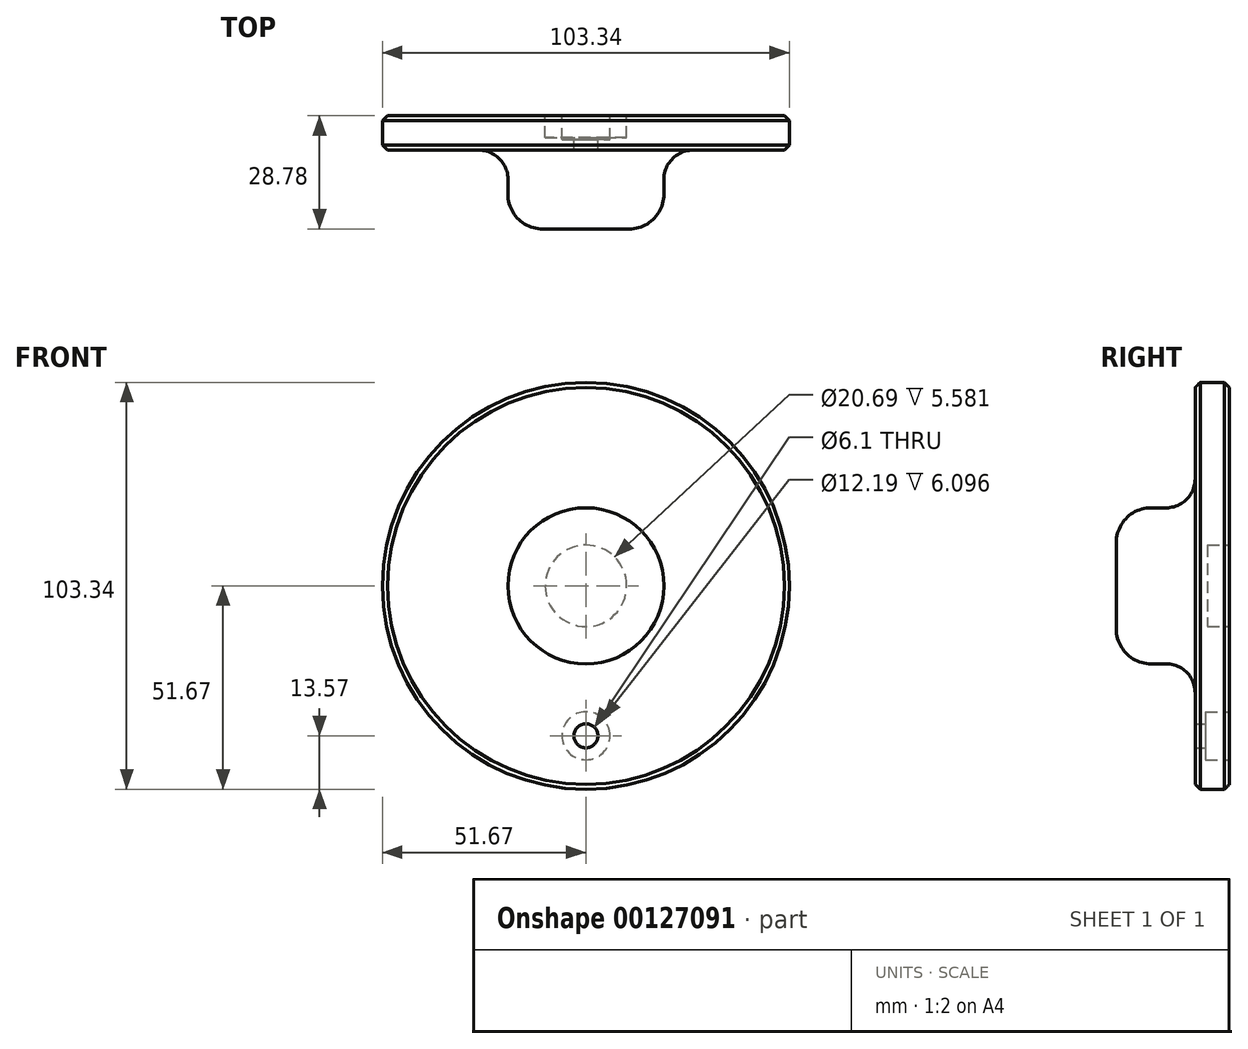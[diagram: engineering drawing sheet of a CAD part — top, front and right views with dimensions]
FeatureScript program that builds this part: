
annotation { "Feature Type Name" : "Feature", "Feature Type Description" : "" }
export const myFeature = defineFeature(function(context is Context, id is Id, definition is map)
    precondition{}
    {
        {
            var Q0;
            Q0=qCreatedBy(makeId("Top.planeOp"),FACE);
            var sketch = newSketch(context, id + "F0", { "sketchPlane" : qUnion([Q0])});
            skLineSegment(sketch, "E0", {"start": v(0, 0) * mm, "end": v(0, 40.3) * mm, "construction": true});
            skSolve(sketch);
        }
        {
            var Q0;
            Q0=qCreatedBy(makeId("Top.planeOp"),FACE);
            var sketch = newSketch(context, id + "F1", { "sketchPlane" : qUnion([Q0])});
            skLineSegment(sketch, "E1", {"start": v(0, 0) * mm, "end": v(19.82, 0) * mm});
            skLineSegment(sketch, "E2", {"start": v(19.82, 0) * mm, "end": v(19.82, 20.03) * mm});
            skLineSegment(sketch, "E3", {"start": v(19.82, 20.03) * mm, "end": v(51.67, 20.03) * mm});
            skLineSegment(sketch, "E4", {"start": v(51.67, 20.03) * mm, "end": v(51.67, 28.78) * mm});
            skLineSegment(sketch, "E5", {"start": v(51.67, 28.78) * mm, "end": v(10.34, 28.78) * mm});
            skLineSegment(sketch, "E6", {"start": v(10.34, 28.78) * mm, "end": v(10.34, 23.2) * mm});
            skLineSegment(sketch, "E7", {"start": v(10.34, 23.2) * mm, "end": v(0, 23.2) * mm});
            skLineSegment(sketch, "E8", {"start": v(0, 23.2) * mm, "end": v(0, 0) * mm});
            skLineSegment(sketch, "E9", {"start": v(0, 23.2) * mm, "end": v(0, 29.85) * mm, "construction": true});
            skSolve(sketch);
        }
        {
            var Q0;
            Q0=makeQuery(id+"F1.imprint","IMPRINT",FACE,{"disambiguationData":[TD([[makeQuery(id+"F1.imprint","IMPRINT",EDGE,{"derivedFrom":sQuery(id+"F1.wireOp",EDGE,"E1")}),1.0]])]});
            var Q1;
            Q1=sQuery(id+"F1.wireOp",EDGE,"E9");
            var Q2;
            Q2=sQuery(id+"F1.wireOp",EDGE,"E6");
            var Q3;
            Q3=sQuery(id+"F1.wireOp",EDGE,"E5");
            var Q4;
            Q4=sQuery(id+"F1.wireOp",EDGE,"E4");
            var Q5;
            Q5=sQuery(id+"F1.wireOp",EDGE,"E3");
            var Q6;
            Q6=sQuery(id+"F1.wireOp",EDGE,"E2");
            var Q7;
            Q7=sQuery(id+"F1.wireOp",EDGE,"E1");
            var Q8;
            Q8=sQuery(id+"F1.wireOp",EDGE,"E7");
            var Q9;
            Q9=sQuery(id+"F1.wireOp",EDGE,"E8");
            revolve(context, id + "F2", {"entities" : qUnion([Q0]), "surfaceEntities" : qUnion([Q1, Q2, Q3, Q4, Q5, Q6, Q7, Q8]), "axis" : qUnion([Q9]), "revolveType" : RevolveType.FULL});
        }
        {
            var Q0;
            Q0=makeQuery(id+"F2.opRevolve","SWEPT_FACE",FACE,{"disambiguationData":[OSD([sQuery(id+"F1.wireOp",EDGE,"E5")])]});
            var sketch = newSketch(context, id + "F3", { "sketchPlane" : qUnion([Q0])});
            skLineSegment(sketch, "E10", {"start": v(0, 0) * mm, "end": v(0, -63.16) * mm, "construction": true});
            skCircle(sketch, "E11", {"center": v(0, 0) * mm, "radius": 38.1 * mm, "construction": true});
            skCircle(sketch, "E12", {"center": v(0, -38.1) * mm, "radius": 6.36 * mm});
            skSolve(sketch);
        }
        {
            var Q0;
            Q0=sQuery(id+"F3.wireOp",VERTEX,"E12.center");
            var Q1;
            Q1=makeQuery(id+"F2.opRevolve","SWEPT_BODY",BODY,{"disambiguationData":[OSD([sQuery(id+"F1.wireOp",EDGE,"E1"),sQuery(id+"F1.wireOp",EDGE,"E2"),sQuery(id+"F1.wireOp",EDGE,"E3"),sQuery(id+"F1.wireOp",EDGE,"E4"),sQuery(id+"F1.wireOp",EDGE,"E5"),sQuery(id+"F1.wireOp",EDGE,"E6"),sQuery(id+"F1.wireOp",EDGE,"E7"),sQuery(id+"F1.wireOp",EDGE,"E8")])]});
            hole(context, id + "F4", {"style" : HoleStyle.C_BORE, "endStyle" : HoleEndStyle.THROUGH, "holeDiameter" : 6.1 * mm, "cBoreDiameter" : 12.2 * mm, "cBoreDepth" : 6.1 * mm, "isTappedThrough" : true, "tappedDepth" : 12.2 * mm, "tapClearance" : 3, "startFromSketch" : true, "locations" : qUnion([Q0]), "scope" : qUnion([Q1])});
        }
        {
            var Q0;
            Q0=makeQuery(id+"F2.opRevolve","SWEPT_EDGE",EDGE,{"disambiguationData":[OSD([sQuery(id+"F1.wireOp",EDGE,"E2"),sQuery(id+"F1.wireOp",EDGE,"E3")])]});
            fillet(context, id + "F5", {"entities" : qUnion([Q0]), "radius" : 7.36 * mm, "tangentPropagation" : true, "allowEdgeOverflow" : false});
        }
        {
            var Q0;
            Q0=makeQuery(id+"F2.opRevolve","SWEPT_EDGE",EDGE,{"disambiguationData":[OSD([sQuery(id+"F1.wireOp",EDGE,"E1"),sQuery(id+"F1.wireOp",EDGE,"E2")])]});
            fillet(context, id + "F6", {"entities" : qUnion([Q0]), "radius" : 8.83 * mm, "tangentPropagation" : true, "allowEdgeOverflow" : false});
        }
        {
            var Q0;
            Q0=makeQuery(id+"F2.opRevolve","SWEPT_EDGE",EDGE,{"disambiguationData":[OSD([sQuery(id+"F1.wireOp",EDGE,"E3"),sQuery(id+"F1.wireOp",EDGE,"E4")])]});
            var Q1;
            Q1=makeQuery(id+"F2.opRevolve","SWEPT_EDGE",EDGE,{"disambiguationData":[OSD([sQuery(id+"F1.wireOp",EDGE,"E4"),sQuery(id+"F1.wireOp",EDGE,"E5")])]});
            chamfer(context, id + "F7", {"entities" : qUnion([Q0, Q1]), "width" : 1.27 * mm, "tangentPropagation" : true});
        }
    });
